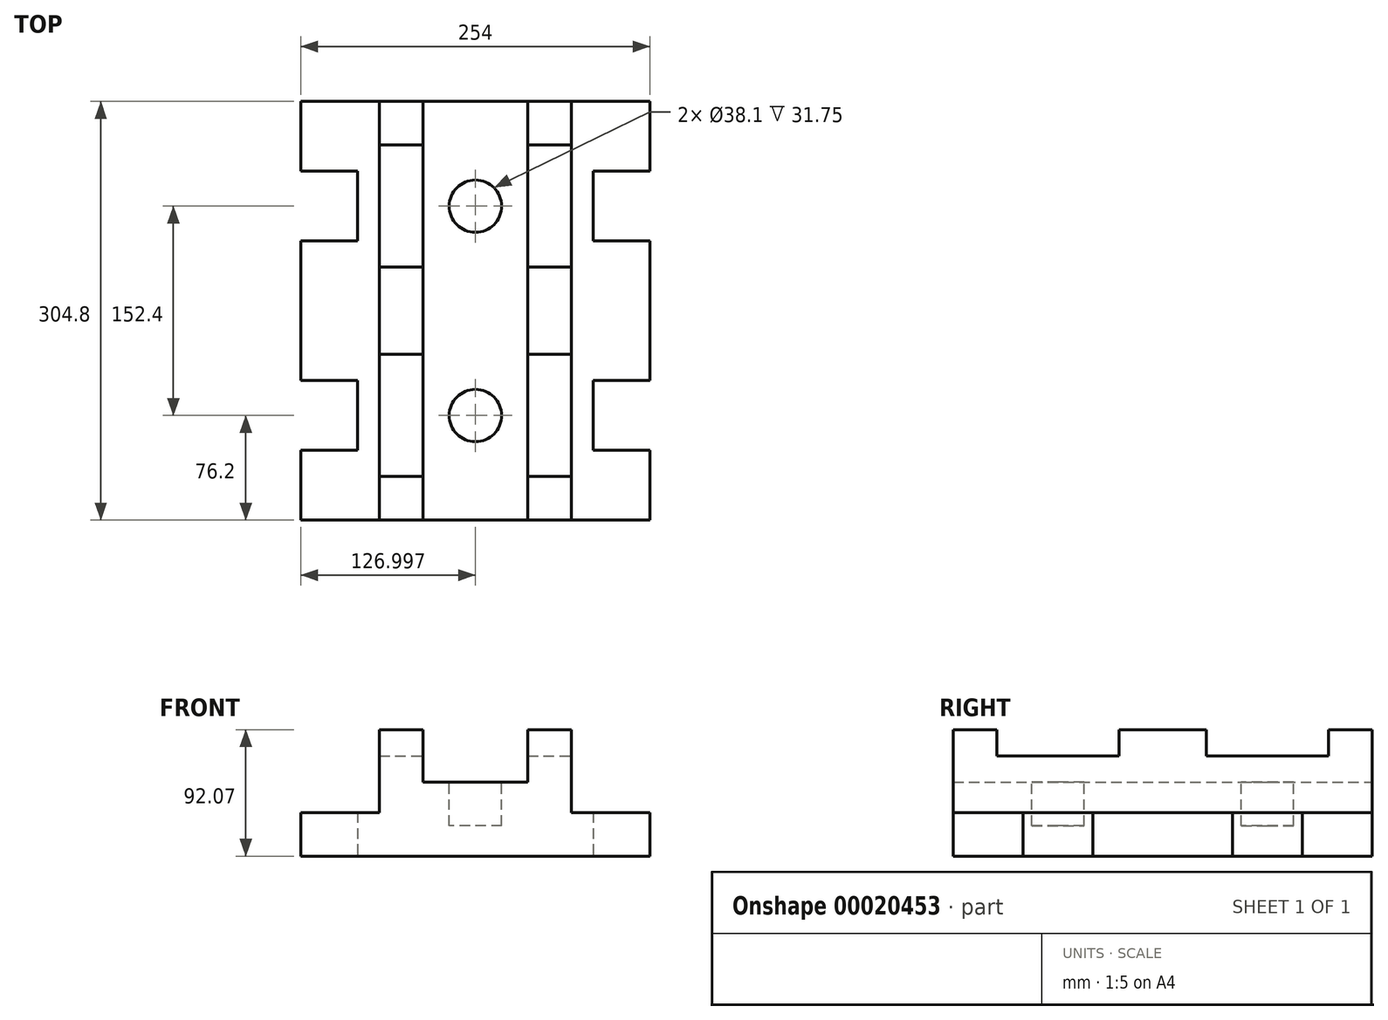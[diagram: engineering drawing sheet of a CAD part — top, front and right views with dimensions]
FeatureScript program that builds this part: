
annotation { "Feature Type Name" : "Feature", "Feature Type Description" : "" }
export const myFeature = defineFeature(function(context is Context, id is Id, definition is map)
    precondition{}
    {
        {
            var Q0;
            Q0=qCreatedBy(makeId("Front.planeOp"),FACE);
            var sketch = newSketch(context, id + "F0", { "sketchPlane" : qUnion([Q0])});
            skLineSegment(sketch, "E0", {"start": v(-138.47, -54.38) * mm, "end": v(115.53, -54.38) * mm});
            skLineSegment(sketch, "E1", {"start": v(-138.47, -54.38) * mm, "end": v(-138.47, -22.63) * mm});
            skLineSegment(sketch, "E2", {"start": v(115.53, -54.38) * mm, "end": v(115.53, -22.63) * mm});
            skLineSegment(sketch, "E3", {"start": v(-138.47, -22.63) * mm, "end": v(-81.32, -22.63) * mm});
            skLineSegment(sketch, "E4", {"start": v(115.53, -22.63) * mm, "end": v(58.38, -22.63) * mm});
            skLineSegment(sketch, "E5", {"start": v(-81.32, -22.63) * mm, "end": v(-81.32, 37.7) * mm});
            skLineSegment(sketch, "E6", {"start": v(-81.32, 37.7) * mm, "end": v(-49.57, 37.7) * mm});
            skLineSegment(sketch, "E7", {"start": v(-49.57, 37.7) * mm, "end": v(-49.57, -0.4) * mm});
            skLineSegment(sketch, "E8", {"start": v(-49.57, -0.4) * mm, "end": v(26.63, -0.4) * mm});
            skLineSegment(sketch, "E9", {"start": v(26.63, -0.4) * mm, "end": v(26.63, 37.7) * mm});
            skLineSegment(sketch, "E10", {"start": v(26.63, 37.7) * mm, "end": v(58.38, 37.7) * mm});
            skLineSegment(sketch, "E11", {"start": v(58.38, 37.7) * mm, "end": v(58.38, -22.63) * mm});
            skSolve(sketch);
        }
        {
            var Q0;
            Q0=makeQuery(id+"F0.imprint","IMPRINT",FACE,{"disambiguationData":[TD([[makeQuery(id+"F0.imprint","IMPRINT",EDGE,{"derivedFrom":sQuery(id+"F0.wireOp",EDGE,"E0")}),1.0]])]});
            extrude(context, id + "F1", {"entities" : qUnion([Q0]), "depth" : 152.4 * mm});
        }
        {
            var Q0;
            Q0=makeQuery(id+"F1.opExtrude","SWEPT_FACE",FACE,{"disambiguationData":[OSD([sQuery(id+"F0.wireOp",EDGE,"E6")])]});
            var sketch = newSketch(context, id + "F2", { "sketchPlane" : qUnion([Q0])});
            skLineSegment(sketch, "E12", {"start": v(-81.32, -31.75) * mm, "end": v(-49.57, -31.75) * mm});
            skLineSegment(sketch, "E13", {"start": v(-49.57, -120.65) * mm, "end": v(-81.32, -120.65) * mm});
            skSolve(sketch);
        }
        {
            var Q0;
            Q0=makeQuery(id+"F1.opExtrude","SWEPT_FACE",FACE,{"disambiguationData":[OSD([sQuery(id+"F0.wireOp",EDGE,"E10")])]});
            var sketch = newSketch(context, id + "F3", { "sketchPlane" : qUnion([Q0])});
            skLineSegment(sketch, "E14", {"start": v(26.63, -31.75) * mm, "end": v(58.38, -31.75) * mm});
            skLineSegment(sketch, "E15", {"start": v(26.63, -120.65) * mm, "end": v(58.38, -120.65) * mm});
            skSolve(sketch);
        }
        {
            var Q0;
            {var subQ3=sQuery(id+"F2.wireOp",EDGE,"E12");Q0=makeQuery(id+"F2.imprint","IMPRINT",FACE,{"disambiguationData":[TD([[makeQuery(id+"F2.imprint","IMPRINT",EDGE,{"derivedFrom":subQ3}),-1.0]])]});}
            var Q1;
            {var subQ3=sQuery(id+"F3.wireOp",EDGE,"E14");Q1=makeQuery(id+"F3.imprint","IMPRINT",FACE,{"disambiguationData":[TD([[makeQuery(id+"F3.imprint","IMPRINT",EDGE,{"derivedFrom":subQ3}),-1.0]])]});}
            extrude(context, id + "F4", {"entities" : qUnion([Q0, Q1]), "operationType" : NewBodyOperationType.REMOVE, "oppositeDirection" : true, "depth" : 19.05 * mm});
        }
        {
            var Q0;
            Q0=makeQuery(id+"F1.opExtrude","SWEPT_FACE",FACE,{"disambiguationData":[OSD([sQuery(id+"F0.wireOp",EDGE,"E2")])]});
            var sketch = newSketch(context, id + "F5", { "sketchPlane" : qUnion([Q0])});
            skLineSegment(sketch, "E16", {"start": v(-101.6, -22.63) * mm, "end": v(-101.6, -54.38) * mm});
            skLineSegment(sketch, "E17", {"start": v(-50.8, -22.63) * mm, "end": v(-50.8, -54.38) * mm});
            skSolve(sketch);
        }
        {
            var Q0;
            Q0=makeQuery(id+"F1.opExtrude","SWEPT_FACE",FACE,{"disambiguationData":[OSD([sQuery(id+"F0.wireOp",EDGE,"E1")])]});
            var sketch = newSketch(context, id + "F6", { "sketchPlane" : qUnion([Q0])});
            skLineSegment(sketch, "E18", {"start": v(50.8, -22.63) * mm, "end": v(50.8, -54.38) * mm});
            skLineSegment(sketch, "E19", {"start": v(101.6, -22.63) * mm, "end": v(101.6, -54.38) * mm});
            skSolve(sketch);
        }
        {
            var Q0;
            {var subQ3=sQuery(id+"F6.wireOp",EDGE,"E18");Q0=makeQuery(id+"F6.imprint","IMPRINT",FACE,{"disambiguationData":[TD([[makeQuery(id+"F6.imprint","IMPRINT",EDGE,{"derivedFrom":subQ3}),1.0]])]});}
            extrude(context, id + "F7", {"entities" : qUnion([Q0]), "operationType" : NewBodyOperationType.REMOVE, "oppositeDirection" : true, "depth" : 41.27 * mm});
        }
        {
            var Q0;
            {var subQ3=sQuery(id+"F5.wireOp",EDGE,"E16");Q0=makeQuery(id+"F5.imprint","IMPRINT",FACE,{"disambiguationData":[TD([[makeQuery(id+"F5.imprint","IMPRINT",EDGE,{"derivedFrom":subQ3}),1.0]])]});}
            extrude(context, id + "F8", {"entities" : qUnion([Q0]), "operationType" : NewBodyOperationType.REMOVE, "oppositeDirection" : true, "depth" : 41.27 * mm});
        }
        {
            var Q0;
            Q0=makeQuery(id+"F1.opExtrude","SWEPT_FACE",FACE,{"disambiguationData":[OSD([sQuery(id+"F0.wireOp",EDGE,"E8")])]});
            var sketch = newSketch(context, id + "F9", { "sketchPlane" : qUnion([Q0])});
            skCircle(sketch, "E20", {"center": v(-11.47, -76.2) * mm, "radius": 19.05 * mm});
            skSolve(sketch);
        }
        {
            var Q0;
            Q0=makeQuery(id+"F9.imprint","IMPRINT",FACE,{"disambiguationData":[TD([[makeQuery(id+"F9.imprint","IMPRINT",EDGE,{"derivedFrom":sQuery(id+"F9.wireOp",EDGE,"E20")}),1.0]])]});
            extrude(context, id + "F10", {"entities" : qUnion([Q0]), "operationType" : NewBodyOperationType.REMOVE, "oppositeDirection" : true, "depth" : 31.75 * mm});
        }
        {
            var Q0;
            Q0=makeQuery(id+"F1.opExtrude","SWEPT_BODY",BODY,{"disambiguationData":[OSD([sQuery(id+"F0.wireOp",EDGE,"E0"),sQuery(id+"F0.wireOp",EDGE,"E1"),sQuery(id+"F0.wireOp",EDGE,"E2"),sQuery(id+"F0.wireOp",EDGE,"E3"),sQuery(id+"F0.wireOp",EDGE,"E4"),sQuery(id+"F0.wireOp",EDGE,"E5"),sQuery(id+"F0.wireOp",EDGE,"E6"),sQuery(id+"F0.wireOp",EDGE,"E7"),sQuery(id+"F0.wireOp",EDGE,"E8"),sQuery(id+"F0.wireOp",EDGE,"E9"),sQuery(id+"F0.wireOp",EDGE,"E10"),sQuery(id+"F0.wireOp",EDGE,"E11")])]});
            var Q1;
            Q1=makeQuery(id+"F1.opExtrude","CAP_FACE",FACE,{"disambiguationData":[OSD([sQuery(id+"F0.wireOp",EDGE,"E0"),sQuery(id+"F0.wireOp",EDGE,"E1"),sQuery(id+"F0.wireOp",EDGE,"E2"),sQuery(id+"F0.wireOp",EDGE,"E3"),sQuery(id+"F0.wireOp",EDGE,"E4"),sQuery(id+"F0.wireOp",EDGE,"E5"),sQuery(id+"F0.wireOp",EDGE,"E6"),sQuery(id+"F0.wireOp",EDGE,"E7"),sQuery(id+"F0.wireOp",EDGE,"E8"),sQuery(id+"F0.wireOp",EDGE,"E9"),sQuery(id+"F0.wireOp",EDGE,"E10"),sQuery(id+"F0.wireOp",EDGE,"E11")])],"isStart":false});
            mirror(context, id + "F11", {"operationType" : NewBodyOperationType.ADD, "entities" : qUnion([Q0]), "mirrorPlane" : qUnion([Q1])});
        }
    });
